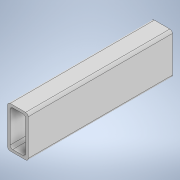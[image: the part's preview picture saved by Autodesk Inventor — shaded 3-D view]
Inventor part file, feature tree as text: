
AUTODESK INVENTOR PART (.ipt)
format: ipt  version: 2020 (Build 240168000, 168)  size: 120,832 bytes
history: native  units: in
note: dims shown in document units (in); Inventor stores cm internally (conversion verified against a paired STEP export)
features: extrude x1, sketch x1
ambient origin geometry x8: Origin, YZ Plane, XZ Plane, XY Plane, X Axis, Y Axis, Z Axis, Center Point
bodies: Solid1 (feature_tree)
feature tree (2):
  extrude  "Extrusion1"  Depth=1.0in
  sketch  "Sketch1"  dims[d0=2.0in d1=1.0in d2=0.125in d3=0.125in d4=0.125in d5=0.125in d6=0.125in d7=0.125in d8=0.125in d9=0.125in d10=0.125in d11=7.0in d12=0.0in]
